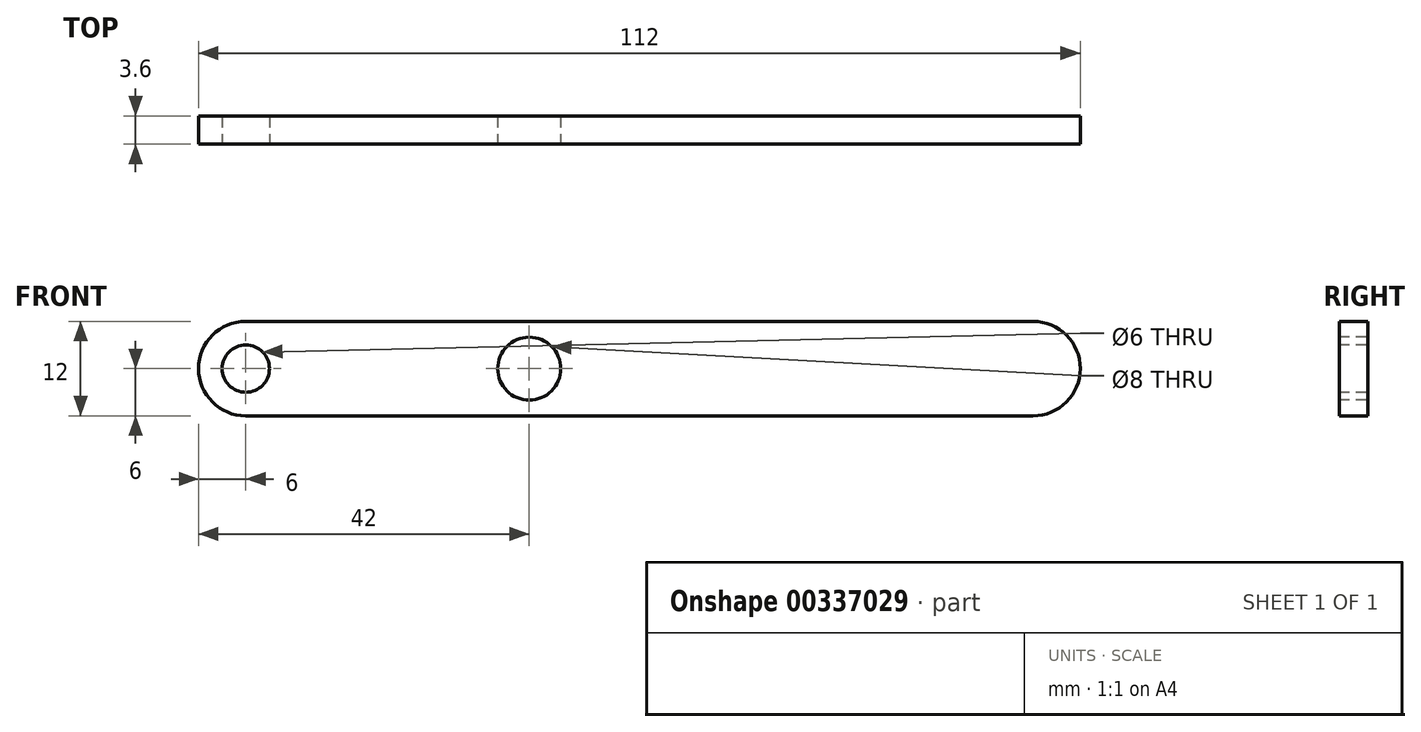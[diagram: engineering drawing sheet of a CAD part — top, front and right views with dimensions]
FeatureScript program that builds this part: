
annotation { "Feature Type Name" : "Feature", "Feature Type Description" : "" }
export const myFeature = defineFeature(function(context is Context, id is Id, definition is map)
    precondition{}
    {
        {
            var Q0;
            Q0=qCreatedBy(makeId("Front.planeOp"),FACE);
            var sketch = newSketch(context, id + "F0", { "sketchPlane" : qUnion([Q0])});
            skLineSegment(sketch, "E0", {"start": v(-50, 6) * mm, "end": v(50, 6) * mm});
            skLineSegment(sketch, "E1", {"start": v(50, 6) * mm, "end": v(50, -6) * mm, "construction": true});
            skLineSegment(sketch, "E2", {"start": v(50, -6) * mm, "end": v(-50, -6) * mm});
            skLineSegment(sketch, "E3", {"start": v(-50, -6) * mm, "end": v(-50, 6) * mm, "construction": true});
            skArc(sketch, "E4", {"start": v(-50, -6) * mm, "mid": v(-56, 0) * mm, "end": v(-50, 6) * mm});
            skArc(sketch, "E5", {"start": v(50, 6) * mm, "mid": v(56, 0) * mm, "end": v(50, -6) * mm});
            skSolve(sketch);
        }
        {
            var Q0;
            Q0=makeQuery(id+"F0.imprint","IMPRINT",FACE,{"disambiguationData":[TD([[makeQuery(id+"F0.imprint","IMPRINT",EDGE,{"derivedFrom":sQuery(id+"F0.wireOp",EDGE,"E0")}),-1.0]])]});
            extrude(context, id + "F1", {"entities" : qUnion([Q0]), "depth" : 3.6 * mm});
        }
        {
            var Q0;
            Q0=makeQuery(id+"F1.opExtrude","CAP_FACE",FACE,{"disambiguationData":[OSD([sQuery(id+"F0.wireOp",EDGE,"E0"),sQuery(id+"F0.wireOp",EDGE,"E2"),sQuery(id+"F0.wireOp",EDGE,"E4"),sQuery(id+"F0.wireOp",EDGE,"E5")])],"isStart":false});
            var sketch = newSketch(context, id + "F2", { "sketchPlane" : qUnion([Q0])});
            skCircle(sketch, "E6", {"center": v(-50, 0) * mm, "radius": 3 * mm});
            skSolve(sketch);
        }
        {
            var Q0;
            Q0=makeQuery(id+"F2.imprint","IMPRINT",FACE,{"disambiguationData":[TD([[makeQuery(id+"F2.imprint","IMPRINT",EDGE,{"derivedFrom":sQuery(id+"F2.wireOp",EDGE,"E6")}),1.0]])]});
            var Q1;
            Q1=makeQuery(id+"F2.imprint","IMPRINT",FACE,{"disambiguationData":[TD([[makeQuery(id+"F2.imprint","IMPRINT",EDGE,{"derivedFrom":sQuery(id+"F2.wireOp",EDGE,"334471ab-0c90-4abc-8ddd-7149dc2213be")}),1.0]])]});
            extrude(context, id + "F3", {"entities" : qUnion([Q0, Q1]), "operationType" : NewBodyOperationType.REMOVE, "endBound" : BoundingType.UP_TO_NEXT, "oppositeDirection" : true, "depth" : 25 * mm});
        }
        {
            var Q0;
            Q0=makeQuery(id+"F2.imprint","IMPRINT",FACE,{"disambiguationData":[TD([[makeQuery(id+"F2.imprint","IMPRINT",EDGE,{"derivedFrom":sQuery(id+"F2.wireOp",EDGE,"E6")}),-1.0]])]});
            var sketch = newSketch(context, id + "F4", { "sketchPlane" : qUnion([Q0])});
            skCircle(sketch, "E7", {"center": v(-14, 0) * mm, "radius": 4 * mm});
            skSolve(sketch);
        }
        {
            var Q0;
            Q0 = qSketchRegion(id + "F4", true);
            extrude(context, id + "F5", {"entities" : qUnion([Q0]), "operationType" : NewBodyOperationType.REMOVE, "endBound" : BoundingType.THROUGH_ALL, "oppositeDirection" : true, "depth" : 25 * mm});
        }
    });
